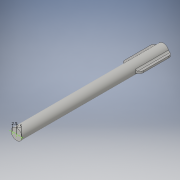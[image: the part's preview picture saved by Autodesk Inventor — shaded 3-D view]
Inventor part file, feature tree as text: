
AUTODESK INVENTOR PART (.ipt)
format: ipt  version: 2016 (Build 200138000, 138)  size: 142,848 bytes
history: native  units: in
note: dims shown in document units (in); Inventor stores cm internally (conversion verified against a paired STEP export)
features: sketch x3, extrude x2, fillet x2
ambient origin geometry x8: Origin, YZ Plane, XZ Plane, XY Plane, X Axis, Y Axis, Z Axis, Center Point
bodies: Solid1 (feature_tree)
feature tree (7):
  extrude  "Extrusion1"  Depth=3.1496in TaperAngle=0.0deg
  extrude  "Extrusion2"  Depth=0.0394in
  fillet  "Fillet1"  Radius=0.7087in
  fillet  "Fillet2"  Radius=0.0394in
  sketch  "Sketch4"  dims[d9=0.1181in d10=0.7087in d11=0.1181in d12=0.0787in d13=0.0394in d24=0.0984in d25=0.0984in]
  sketch  "Sketch1"  dims[d0=0.2362in d1=3.1496in d2=0.0in]
  sketch  "Sketch2"  dims[d3=0.0787in d4=0.0787in d6=0.7087in d7=0.0394in d8=0.0in]
